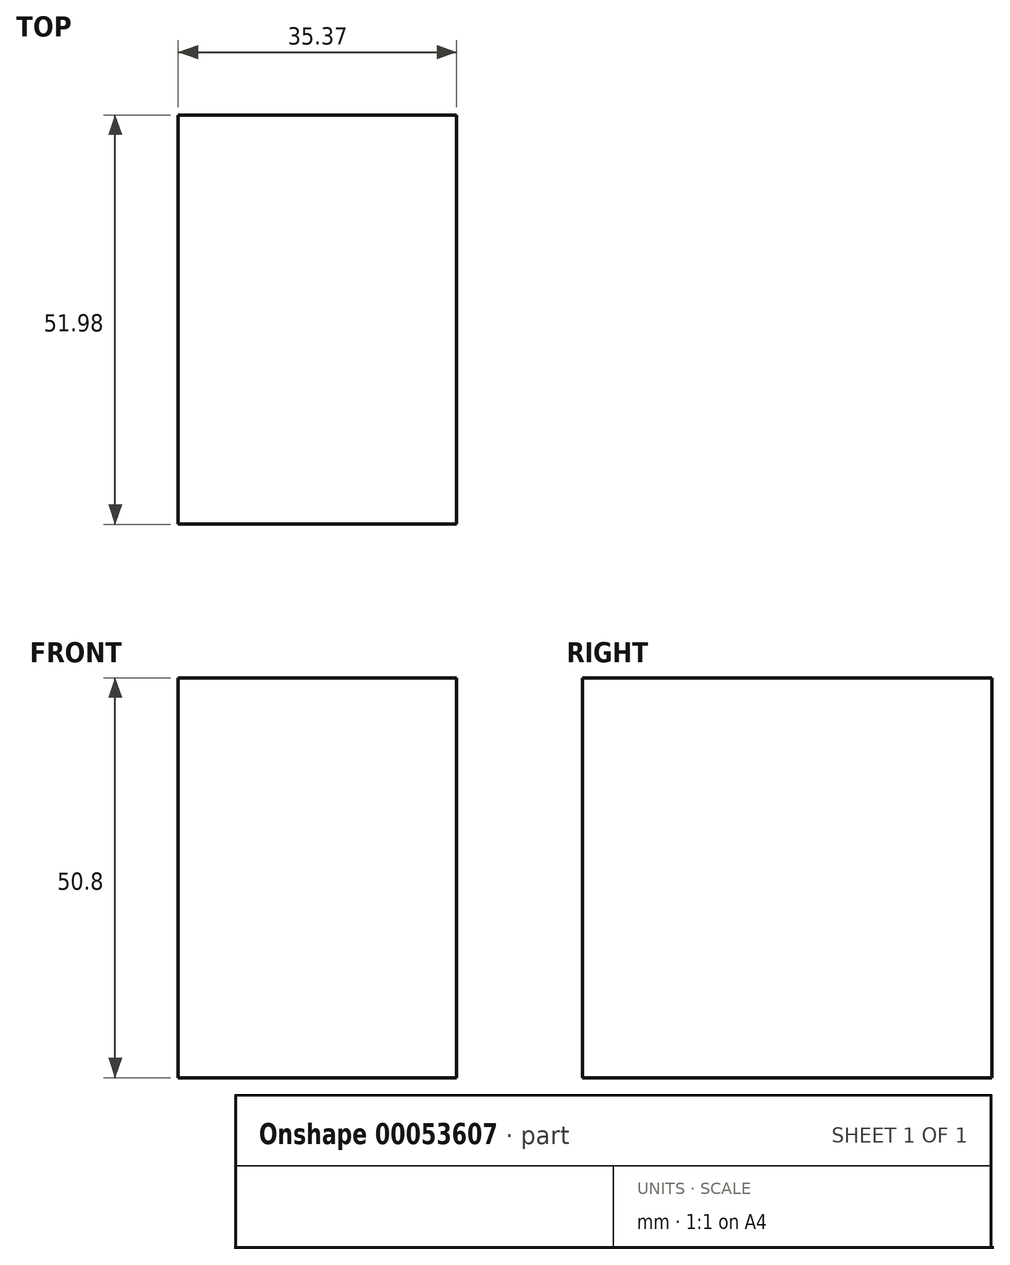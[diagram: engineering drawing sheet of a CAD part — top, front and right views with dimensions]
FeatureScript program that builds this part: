
annotation { "Feature Type Name" : "Feature", "Feature Type Description" : "" }
export const myFeature = defineFeature(function(context is Context, id is Id, definition is map)
    precondition{}
    {
        {
            var Q0;
            Q0=qCreatedBy(makeId("Top.planeOp"),FACE);
            var sketch = newSketch(context, id + "F0", { "sketchPlane" : qUnion([Q0])});
            skLineSegment(sketch, "E0.bottom", {"start": v(-48.54, -28.56) * mm, "end": v(35.37, -28.56) * mm});
            skLineSegment(sketch, "E0.top", {"start": v(-48.54, 55.06) * mm, "end": v(35.37, 55.06) * mm});
            skLineSegment(sketch, "E0.left", {"start": v(-48.54, -28.56) * mm, "end": v(-48.54, 55.06) * mm});
            skLineSegment(sketch, "E0.right", {"start": v(35.37, -28.56) * mm, "end": v(35.37, 55.06) * mm});
            skLineSegment(sketch, "E1.bottom", {"start": v(0, 55.06) * mm, "end": v(35.37, 55.06) * mm});
            skLineSegment(sketch, "E1.top", {"start": v(0, -28.56) * mm, "end": v(35.37, -28.56) * mm});
            skLineSegment(sketch, "E1.left", {"start": v(0, 55.06) * mm, "end": v(0, -28.56) * mm});
            skLineSegment(sketch, "E1.right", {"start": v(35.37, 55.06) * mm, "end": v(35.37, -28.56) * mm});
            skLineSegment(sketch, "E2.bottom", {"start": v(0, 23.42) * mm, "end": v(35.37, 23.42) * mm});
            skLineSegment(sketch, "E2.left", {"start": v(0, 23.42) * mm, "end": v(0, 55.06) * mm});
            skLineSegment(sketch, "E2.right", {"start": v(35.37, 23.42) * mm, "end": v(35.37, 55.06) * mm});
            skSolve(sketch);
        }
        {
            var Q0;
            Q0=makeQuery(id+"F0.imprint","IMPRINT",FACE,{"disambiguationData":[TD([[makeQuery(id+"F0.imprint","IMPRINT",EDGE,{"derivedFrom":sQuery(id+"F0.wireOp",EDGE,"E0.bottom")}),1.0]])]});
            var Q1;
            Q1=makeQuery(id+"F0.imprint","IMPRINT",FACE,{"disambiguationData":[TD([[makeQuery(id+"F0.imprint","IMPRINT",EDGE,{"derivedFrom":sQuery(id+"F0.wireOp",EDGE,"E1.top")}),1.0]])]});
            extrude(context, id + "F1", {"entities" : qUnion([Q0, Q1]), "depth" : 50.8 * mm});
        }
    });
